# Revit family: VA4068881_VERA Mezclador monocontrol SSB
name_source: partatom
category: Plumbing Fixtures
units: mm (PartAtom-declared; Revit-internal decimal feet)

## family parameters
Always vertical = Yes
Cut with Voids When Loaded = No
OmniClass Number = 23.31.15.11
OmniClass Title = Bath Shower Units
Part Type = Normal
Room Calculation Point = No
Round Connector Dimension = Use Diameter
Shared = No
Work Plane-Based = No

## types (1)
- VA4068881_VERA Mezclador monocontrol SSB
    Ciclo de vida de la unidad de cierre = 250.000 ciclos
    Creado por = IDD
    Description = El mezclador monocontrol SSB Vera ha sido diseñada para trabajar en perfecta
armonía con el espacio; inspirada en las necesidades del consumidor latinoamericano
dando como resultado un producto robusto y funcional. Permite regular la temperatura
del agua con una sola manija.
    Dimensiónes generales de producto (H x W x L) = 60 x 321 x 134 mm. / 2,4 x 12,6 x 5,3 pulg
    Fecha de creación = 21/07/2020
    Material = Corona_Plastico_Cromado
    Material. = Plástico
    Peso bruto aproximado = 870gr. / 1,92Lb
    Peso neto aproximado = 759gr. / 1,67Lb
    Presión máxima recomendada = 125 psi
    Presión mínima recomendada = 20 psi
    Recubrimientos = No tóxicos
    Resistencia = Resistente a la corrosión, pelado y decoloración por agua
    Temperaturas máxima de trabajo = 71 ºC / 159,8 ºF
    Temperaturas mínima de trabajo = 5 ºC / 41 ºF
    URL = https://corona.co
    Uso = Productos para uso doméstico
    Vida útil de la junta de bola (Regadera) = 10.000 ciclos

## geometry (parser evidence)
native form markers: Sweep x4
no freeform markers — native parametric forms only
